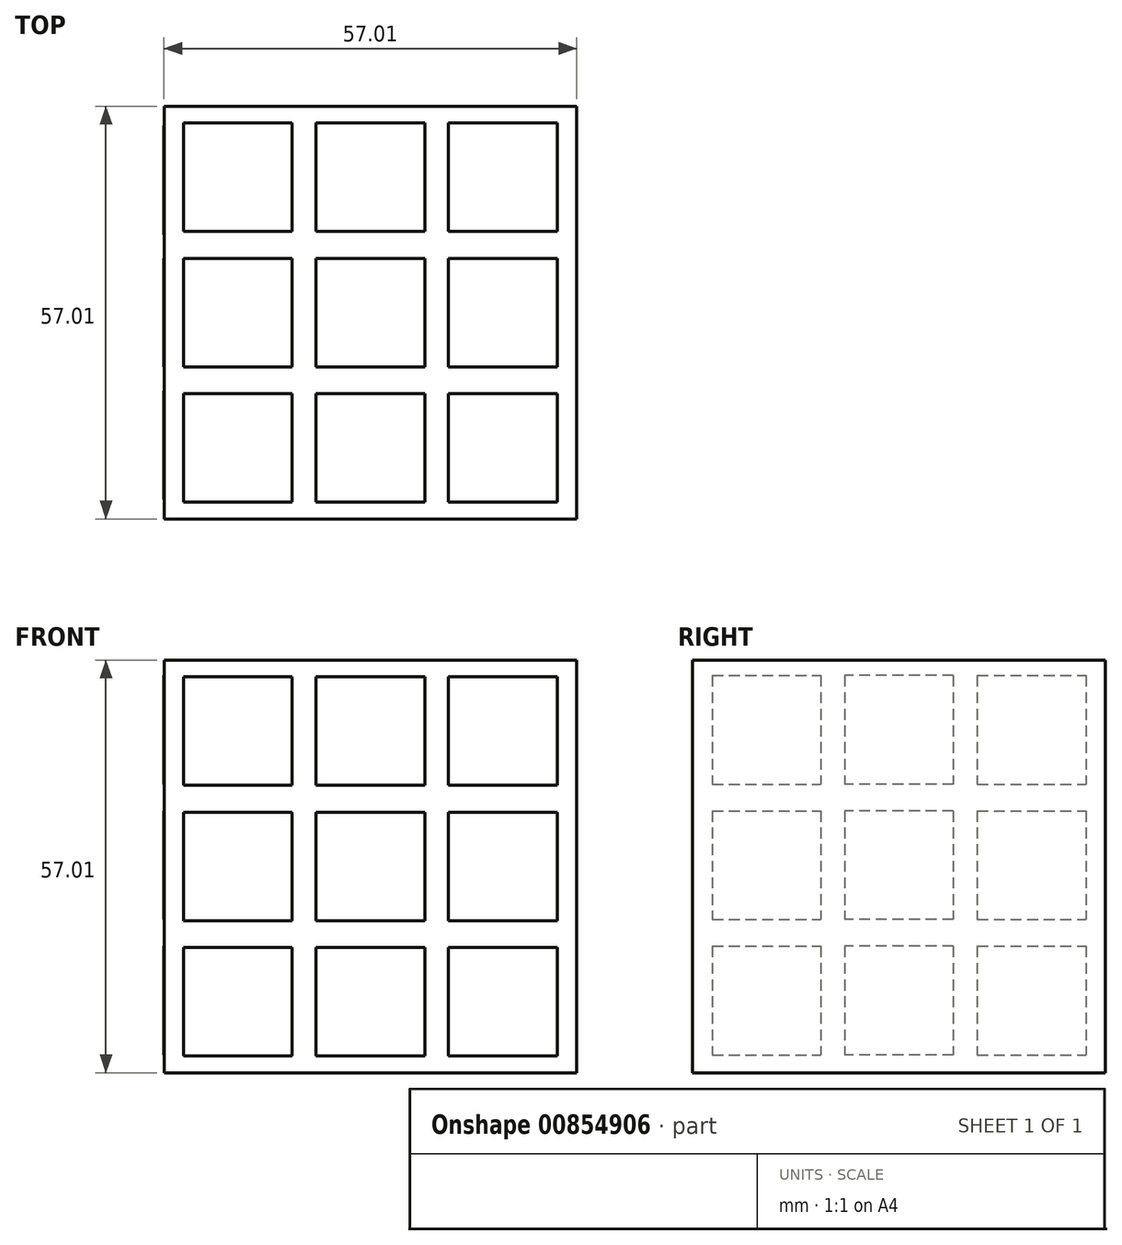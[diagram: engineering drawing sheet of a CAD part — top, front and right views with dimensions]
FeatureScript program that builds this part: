
annotation { "Feature Type Name" : "Feature", "Feature Type Description" : "" }
export const myFeature = defineFeature(function(context is Context, id is Id, definition is map)
    precondition{}
    {
        {
            var Q0;
            Q0=qCreatedBy(makeId("Front.planeOp"),FACE);
            var sketch = newSketch(context, id + "F0", { "sketchPlane" : qUnion([Q0])});
            skLineSegment(sketch, "E0.bottom", {"start": v(-57.56, 22.9) * mm, "end": v(-0.56, 22.9) * mm});
            skLineSegment(sketch, "E0.top", {"start": v(-57.56, -34.1) * mm, "end": v(-0.56, -34.1) * mm});
            skLineSegment(sketch, "E0.left", {"start": v(-57.56, 22.9) * mm, "end": v(-57.56, -34.1) * mm});
            skLineSegment(sketch, "E0.right", {"start": v(-0.56, 22.9) * mm, "end": v(-0.56, -34.1) * mm});
            skSolve(sketch);
        }
        {
            var Q0;
            Q0 = qSketchRegion(id + "F0", true);
            extrude(context, id + "F1", {"entities" : qUnion([Q0]), "depth" : 57 * mm, "offsetDistance" : 25 * mm});
        }
        {
            var Q0;
            Q0=makeQuery(id+"F1.opExtrude","SWEPT_FACE",FACE,{"disambiguationData":[OSD([sQuery(id+"F0.wireOp",EDGE,"E0.bottom")])]});
            var sketch = newSketch(context, id + "F2", { "sketchPlane" : qUnion([Q0])});
            skLineSegment(sketch, "E1.bottom", {"start": v(-3.26, -2.3) * mm, "end": v(-18.26, -2.3) * mm});
            skLineSegment(sketch, "E1.top", {"start": v(-3.26, -17.3) * mm, "end": v(-18.26, -17.3) * mm});
            skLineSegment(sketch, "E1.left", {"start": v(-3.26, -2.3) * mm, "end": v(-3.26, -17.3) * mm});
            skLineSegment(sketch, "E1.right", {"start": v(-18.26, -2.3) * mm, "end": v(-18.26, -17.3) * mm});
            skLineSegment(sketch, "E2.bottom", {"start": v(-3.26, -21) * mm, "end": v(-18.26, -21) * mm});
            skLineSegment(sketch, "E2.top", {"start": v(-3.26, -36) * mm, "end": v(-18.26, -36) * mm});
            skLineSegment(sketch, "E2.left", {"start": v(-3.26, -21) * mm, "end": v(-3.26, -36) * mm});
            skLineSegment(sketch, "E2.right", {"start": v(-18.26, -21) * mm, "end": v(-18.26, -36) * mm});
            skLineSegment(sketch, "E3.bottom", {"start": v(-3.26, -39.7) * mm, "end": v(-18.26, -39.7) * mm});
            skLineSegment(sketch, "E3.top", {"start": v(-3.26, -54.7) * mm, "end": v(-18.26, -54.7) * mm});
            skLineSegment(sketch, "E3.left", {"start": v(-3.26, -39.7) * mm, "end": v(-3.26, -54.7) * mm});
            skLineSegment(sketch, "E3.right", {"start": v(-18.26, -39.7) * mm, "end": v(-18.26, -54.7) * mm});
            skLineSegment(sketch, "E4", {"start": v(-19.91, -57) * mm, "end": v(-19.91, 0) * mm});
            skLineSegment(sketch, "E5.MirrorCS", {"start": v(-36.56, -39.7) * mm, "end": v(-21.56, -39.7) * mm});
            skLineSegment(sketch, "E6.MirrorCS", {"start": v(-21.56, -39.7) * mm, "end": v(-21.56, -54.7) * mm});
            skLineSegment(sketch, "E7.MirrorCS", {"start": v(-36.56, -54.7) * mm, "end": v(-21.56, -54.7) * mm});
            skLineSegment(sketch, "E8.MirrorCS", {"start": v(-36.56, -39.7) * mm, "end": v(-36.56, -54.7) * mm});
            skLineSegment(sketch, "E9.MirrorCS", {"start": v(-36.56, -36) * mm, "end": v(-21.56, -36) * mm});
            skLineSegment(sketch, "E10.MirrorCS", {"start": v(-21.56, -21) * mm, "end": v(-21.56, -36) * mm});
            skLineSegment(sketch, "E11.MirrorCS", {"start": v(-36.56, -21) * mm, "end": v(-21.56, -21) * mm});
            skLineSegment(sketch, "E12.MirrorCS", {"start": v(-36.56, -21) * mm, "end": v(-36.56, -36) * mm});
            skLineSegment(sketch, "E13.MirrorCS", {"start": v(-36.56, -17.3) * mm, "end": v(-21.56, -17.3) * mm});
            skLineSegment(sketch, "E14.MirrorCS", {"start": v(-21.56, -2.3) * mm, "end": v(-21.56, -17.3) * mm});
            skLineSegment(sketch, "E15.MirrorCS", {"start": v(-36.56, -2.3) * mm, "end": v(-21.56, -2.3) * mm});
            skLineSegment(sketch, "E16.MirrorCS", {"start": v(-36.56, -2.3) * mm, "end": v(-36.56, -17.3) * mm});
            skLineSegment(sketch, "E17", {"start": v(-38.21, 0) * mm, "end": v(-38.21, -57) * mm});
            skLineSegment(sketch, "E18.MirrorCS", {"start": v(-39.86, -54.7) * mm, "end": v(-54.86, -54.7) * mm});
            skLineSegment(sketch, "E19.MirrorCS", {"start": v(-39.86, -39.7) * mm, "end": v(-39.86, -54.7) * mm});
            skLineSegment(sketch, "E20.MirrorCS", {"start": v(-39.86, -39.7) * mm, "end": v(-54.86, -39.7) * mm});
            skLineSegment(sketch, "E21.MirrorCS", {"start": v(-54.86, -39.7) * mm, "end": v(-54.86, -54.7) * mm});
            skLineSegment(sketch, "E22.MirrorCS", {"start": v(-39.86, -36) * mm, "end": v(-54.86, -36) * mm});
            skLineSegment(sketch, "E23.MirrorCS", {"start": v(-39.86, -21) * mm, "end": v(-54.86, -21) * mm});
            skLineSegment(sketch, "E24.MirrorCS", {"start": v(-39.86, -21) * mm, "end": v(-39.86, -36) * mm});
            skLineSegment(sketch, "E25.MirrorCS", {"start": v(-54.86, -21) * mm, "end": v(-54.86, -36) * mm});
            skLineSegment(sketch, "E26.MirrorCS", {"start": v(-39.86, -17.3) * mm, "end": v(-54.86, -17.3) * mm});
            skLineSegment(sketch, "E27.MirrorCS", {"start": v(-39.86, -2.3) * mm, "end": v(-54.86, -2.3) * mm});
            skLineSegment(sketch, "E28.MirrorCS", {"start": v(-54.86, -2.3) * mm, "end": v(-54.86, -17.3) * mm});
            skLineSegment(sketch, "E29.MirrorCS", {"start": v(-39.86, -2.3) * mm, "end": v(-39.86, -17.3) * mm});
            skSolve(sketch);
        }
        {
            var Q0;
            Q0 = qSketchRegion(id + "F2", true);
            extrude(context, id + "F3", {"entities" : qUnion([Q0]), "operationType" : NewBodyOperationType.ADD, "depth" : 0.01 * mm, "offsetDistance" : 25 * mm});
        }
        {
            var Q0;
            Q0=makeQuery(id+"F1.opExtrude","CAP_FACE",FACE,{"disambiguationData":[OSD([sQuery(id+"F0.wireOp",EDGE,"E0.bottom"),sQuery(id+"F0.wireOp",EDGE,"E0.top"),sQuery(id+"F0.wireOp",EDGE,"E0.left"),sQuery(id+"F0.wireOp",EDGE,"E0.right")])],"isStart":false});
            var sketch = newSketch(context, id + "F4", { "sketchPlane" : qUnion([Q0])});
            skLineSegment(sketch, "E30.bottom", {"start": v(-3.26, 20.6) * mm, "end": v(-18.26, 20.6) * mm});
            skLineSegment(sketch, "E30.top", {"start": v(-3.26, 5.6) * mm, "end": v(-18.26, 5.6) * mm});
            skLineSegment(sketch, "E30.left", {"start": v(-3.26, 20.6) * mm, "end": v(-3.26, 5.6) * mm});
            skLineSegment(sketch, "E30.right", {"start": v(-18.26, 20.6) * mm, "end": v(-18.26, 5.6) * mm});
            skLineSegment(sketch, "E31.bottom", {"start": v(-3.26, 1.9) * mm, "end": v(-18.26, 1.9) * mm});
            skLineSegment(sketch, "E31.top", {"start": v(-3.26, -13.1) * mm, "end": v(-18.26, -13.1) * mm});
            skLineSegment(sketch, "E31.left", {"start": v(-3.26, 1.9) * mm, "end": v(-3.26, -13.1) * mm});
            skLineSegment(sketch, "E31.right", {"start": v(-18.26, 1.9) * mm, "end": v(-18.26, -13.1) * mm});
            skLineSegment(sketch, "E32.bottom", {"start": v(-3.26, -16.8) * mm, "end": v(-18.26, -16.8) * mm});
            skLineSegment(sketch, "E32.top", {"start": v(-3.26, -31.8) * mm, "end": v(-18.26, -31.8) * mm});
            skLineSegment(sketch, "E32.left", {"start": v(-3.26, -16.8) * mm, "end": v(-3.26, -31.8) * mm});
            skLineSegment(sketch, "E32.right", {"start": v(-18.26, -16.8) * mm, "end": v(-18.26, -31.8) * mm});
            skLineSegment(sketch, "E33", {"start": v(-19.91, -46.05) * mm, "end": v(-19.91, 10.95) * mm});
            skLineSegment(sketch, "E34.MirrorCS", {"start": v(-36.56, -16.8) * mm, "end": v(-21.56, -16.8) * mm});
            skLineSegment(sketch, "E35.MirrorCS", {"start": v(-21.56, -16.8) * mm, "end": v(-21.56, -31.8) * mm});
            skLineSegment(sketch, "E36.MirrorCS", {"start": v(-36.56, -31.8) * mm, "end": v(-21.56, -31.8) * mm});
            skLineSegment(sketch, "E37.MirrorCS", {"start": v(-36.56, -16.8) * mm, "end": v(-36.56, -31.8) * mm});
            skLineSegment(sketch, "E38.MirrorCS", {"start": v(-36.56, -13.1) * mm, "end": v(-21.56, -13.1) * mm});
            skLineSegment(sketch, "E39.MirrorCS", {"start": v(-21.56, 1.9) * mm, "end": v(-21.56, -13.1) * mm});
            skLineSegment(sketch, "E40.MirrorCS", {"start": v(-36.56, 1.9) * mm, "end": v(-21.56, 1.9) * mm});
            skLineSegment(sketch, "E41.MirrorCS", {"start": v(-36.56, 1.9) * mm, "end": v(-36.56, -13.1) * mm});
            skLineSegment(sketch, "E42.MirrorCS", {"start": v(-36.56, 5.6) * mm, "end": v(-21.56, 5.6) * mm});
            skLineSegment(sketch, "E43.MirrorCS", {"start": v(-21.56, 20.6) * mm, "end": v(-21.56, 5.6) * mm});
            skLineSegment(sketch, "E44.MirrorCS", {"start": v(-36.56, 20.6) * mm, "end": v(-21.56, 20.6) * mm});
            skLineSegment(sketch, "E45.MirrorCS", {"start": v(-36.56, 20.6) * mm, "end": v(-36.56, 5.6) * mm});
            skLineSegment(sketch, "E46", {"start": v(-38.21, 22.9) * mm, "end": v(-38.21, -46.05) * mm});
            skLineSegment(sketch, "E47.MirrorCS", {"start": v(-39.86, -31.8) * mm, "end": v(-54.86, -31.8) * mm});
            skLineSegment(sketch, "E48.MirrorCS", {"start": v(-39.86, -16.8) * mm, "end": v(-39.86, -31.8) * mm});
            skLineSegment(sketch, "E49.MirrorCS", {"start": v(-39.86, -16.8) * mm, "end": v(-54.86, -16.8) * mm});
            skLineSegment(sketch, "E50.MirrorCS", {"start": v(-54.86, -16.8) * mm, "end": v(-54.86, -31.8) * mm});
            skLineSegment(sketch, "E51.MirrorCS", {"start": v(-39.86, -13.1) * mm, "end": v(-54.86, -13.1) * mm});
            skLineSegment(sketch, "E52.MirrorCS", {"start": v(-39.86, 1.9) * mm, "end": v(-54.86, 1.9) * mm});
            skLineSegment(sketch, "E53.MirrorCS", {"start": v(-39.86, 1.9) * mm, "end": v(-39.86, -13.1) * mm});
            skLineSegment(sketch, "E54.MirrorCS", {"start": v(-54.86, 1.9) * mm, "end": v(-54.86, -13.1) * mm});
            skLineSegment(sketch, "E55.MirrorCS", {"start": v(-39.86, 5.6) * mm, "end": v(-54.86, 5.6) * mm});
            skLineSegment(sketch, "E56.MirrorCS", {"start": v(-39.86, 20.6) * mm, "end": v(-54.86, 20.6) * mm});
            skLineSegment(sketch, "E57.MirrorCS", {"start": v(-54.86, 20.6) * mm, "end": v(-54.86, 5.6) * mm});
            skLineSegment(sketch, "E58.MirrorCS", {"start": v(-39.86, 20.6) * mm, "end": v(-39.86, 5.6) * mm});
            skSolve(sketch);
        }
        {
            var Q0;
            Q0 = qSketchRegion(id + "F4", true);
            extrude(context, id + "F5", {"entities" : qUnion([Q0]), "operationType" : NewBodyOperationType.ADD, "depth" : 0.01 * mm, "offsetDistance" : 25 * mm});
        }
        {
            var Q0;
            Q0=makeQuery(id+"F1.opExtrude","SWEPT_FACE",FACE,{"disambiguationData":[OSD([sQuery(id+"F0.wireOp",EDGE,"E0.left")])]});
            var sketch = newSketch(context, id + "F6", { "sketchPlane" : qUnion([Q0])});
            skLineSegment(sketch, "E59.bottom", {"start": v(54.3, 20.77) * mm, "end": v(39.3, 20.77) * mm});
            skLineSegment(sketch, "E59.top", {"start": v(54.3, 5.77) * mm, "end": v(39.3, 5.77) * mm});
            skLineSegment(sketch, "E59.left", {"start": v(54.3, 20.77) * mm, "end": v(54.3, 5.77) * mm});
            skLineSegment(sketch, "E59.right", {"start": v(39.3, 20.77) * mm, "end": v(39.3, 5.77) * mm});
            skLineSegment(sketch, "E60.bottom", {"start": v(54.3, 2.07) * mm, "end": v(39.3, 2.07) * mm});
            skLineSegment(sketch, "E60.top", {"start": v(54.3, -12.93) * mm, "end": v(39.3, -12.93) * mm});
            skLineSegment(sketch, "E60.left", {"start": v(54.3, 2.07) * mm, "end": v(54.3, -12.93) * mm});
            skLineSegment(sketch, "E60.right", {"start": v(39.3, 2.07) * mm, "end": v(39.3, -12.93) * mm});
            skLineSegment(sketch, "E61.bottom", {"start": v(54.3, -16.63) * mm, "end": v(39.3, -16.63) * mm});
            skLineSegment(sketch, "E61.top", {"start": v(54.3, -31.63) * mm, "end": v(39.3, -31.63) * mm});
            skLineSegment(sketch, "E61.left", {"start": v(54.3, -16.63) * mm, "end": v(54.3, -31.63) * mm});
            skLineSegment(sketch, "E61.right", {"start": v(39.3, -16.63) * mm, "end": v(39.3, -31.63) * mm});
            skLineSegment(sketch, "E62", {"start": v(37.65, -31.8) * mm, "end": v(37.65, 11.13) * mm});
            skLineSegment(sketch, "E63.MirrorCS", {"start": v(21, -16.63) * mm, "end": v(36, -16.63) * mm});
            skLineSegment(sketch, "E64.MirrorCS", {"start": v(36, -16.63) * mm, "end": v(36, -31.63) * mm});
            skLineSegment(sketch, "E65.MirrorCS", {"start": v(21, -31.63) * mm, "end": v(36, -31.63) * mm});
            skLineSegment(sketch, "E66.MirrorCS", {"start": v(21, -16.63) * mm, "end": v(21, -31.63) * mm});
            skLineSegment(sketch, "E67.MirrorCS", {"start": v(21, -12.93) * mm, "end": v(36, -12.93) * mm});
            skLineSegment(sketch, "E68.MirrorCS", {"start": v(36, 2.07) * mm, "end": v(36, -12.93) * mm});
            skLineSegment(sketch, "E69.MirrorCS", {"start": v(21, 2.07) * mm, "end": v(36, 2.07) * mm});
            skLineSegment(sketch, "E70.MirrorCS", {"start": v(21, 2.07) * mm, "end": v(21, -12.93) * mm});
            skLineSegment(sketch, "E71.MirrorCS", {"start": v(21, 5.77) * mm, "end": v(36, 5.77) * mm});
            skLineSegment(sketch, "E72.MirrorCS", {"start": v(36, 20.77) * mm, "end": v(36, 5.77) * mm});
            skLineSegment(sketch, "E73.MirrorCS", {"start": v(21, 20.77) * mm, "end": v(36, 20.77) * mm});
            skLineSegment(sketch, "E74.MirrorCS", {"start": v(21, 20.77) * mm, "end": v(21, 5.77) * mm});
            skLineSegment(sketch, "E75", {"start": v(19.35, 23.07) * mm, "end": v(19.35, -45.87) * mm});
            skLineSegment(sketch, "E76.MirrorCS", {"start": v(17.7, -31.63) * mm, "end": v(2.7, -31.63) * mm});
            skLineSegment(sketch, "E77.MirrorCS", {"start": v(17.7, -16.63) * mm, "end": v(17.7, -31.63) * mm});
            skLineSegment(sketch, "E78.MirrorCS", {"start": v(17.7, -16.63) * mm, "end": v(2.7, -16.63) * mm});
            skLineSegment(sketch, "E79.MirrorCS", {"start": v(2.7, -16.63) * mm, "end": v(2.7, -31.63) * mm});
            skLineSegment(sketch, "E80.MirrorCS", {"start": v(17.7, -12.93) * mm, "end": v(2.7, -12.93) * mm});
            skLineSegment(sketch, "E81.MirrorCS", {"start": v(17.7, 2.07) * mm, "end": v(2.7, 2.07) * mm});
            skLineSegment(sketch, "E82.MirrorCS", {"start": v(17.7, 2.07) * mm, "end": v(17.7, -12.93) * mm});
            skLineSegment(sketch, "E83.MirrorCS", {"start": v(2.7, 2.07) * mm, "end": v(2.7, -12.93) * mm});
            skLineSegment(sketch, "E84.MirrorCS", {"start": v(17.7, 5.77) * mm, "end": v(2.7, 5.77) * mm});
            skLineSegment(sketch, "E85.MirrorCS", {"start": v(17.7, 20.77) * mm, "end": v(2.7, 20.77) * mm});
            skLineSegment(sketch, "E86.MirrorCS", {"start": v(2.7, 20.77) * mm, "end": v(2.7, 5.77) * mm});
            skLineSegment(sketch, "E87.MirrorCS", {"start": v(17.7, 20.77) * mm, "end": v(17.7, 5.77) * mm});
            skSolve(sketch);
        }
        {
            var Q0;
            Q0 = qSketchRegion(id + "F6", true);
            extrude(context, id + "F7", {"entities" : qUnion([Q0]), "operationType" : NewBodyOperationType.ADD, "depth" : 0.01 * mm, "offsetDistance" : 25 * mm});
        }
    });
